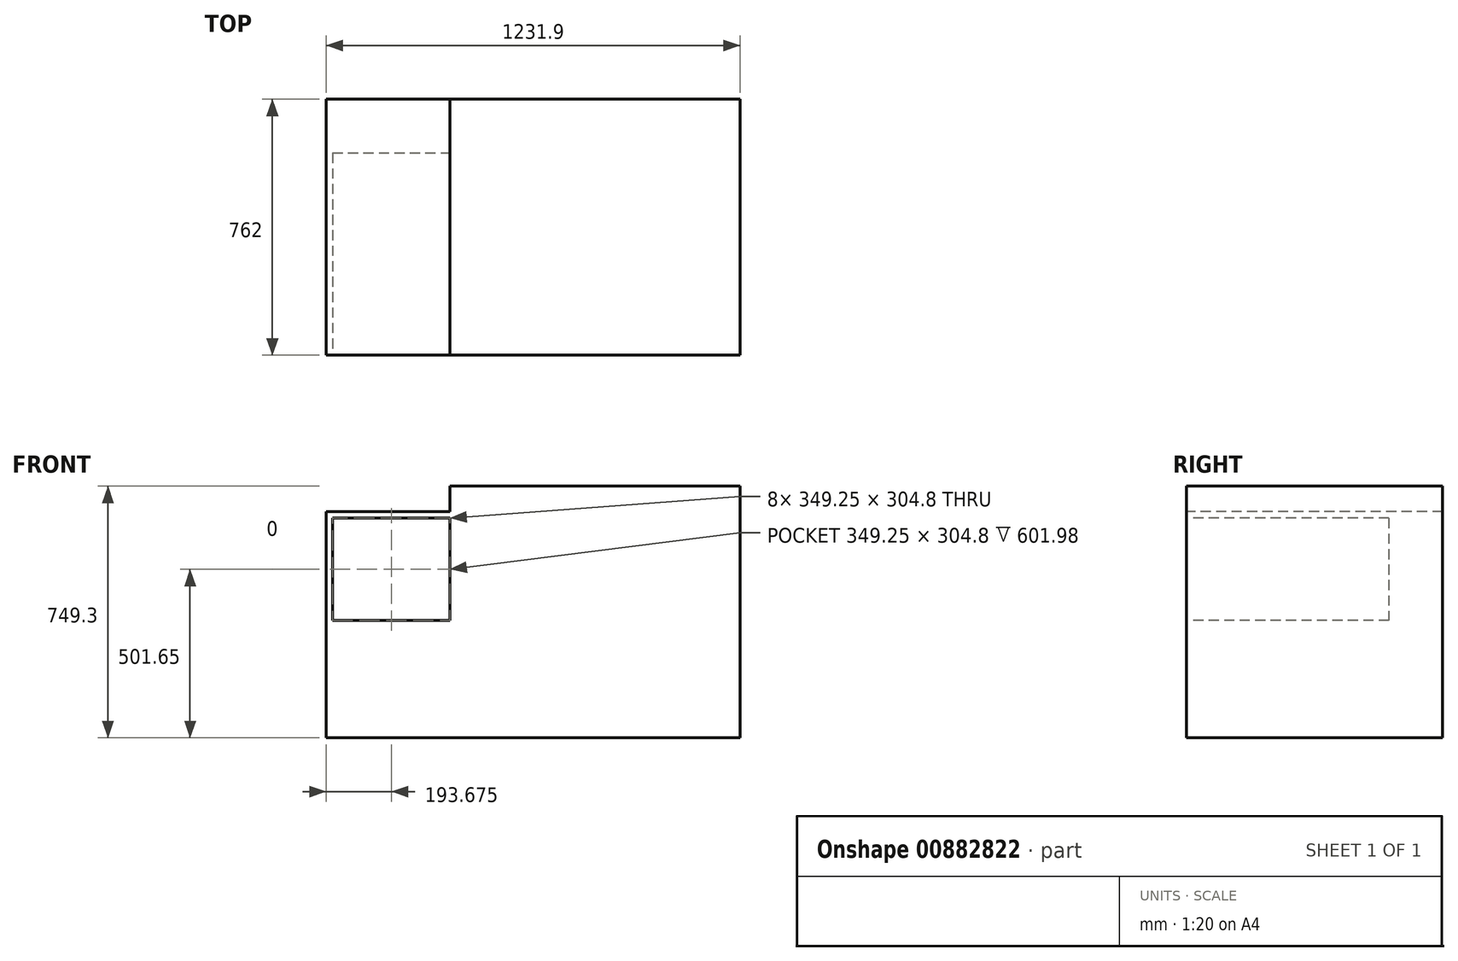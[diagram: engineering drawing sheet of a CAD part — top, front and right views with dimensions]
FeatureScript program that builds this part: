
annotation { "Feature Type Name" : "Feature", "Feature Type Description" : "" }
export const myFeature = defineFeature(function(context is Context, id is Id, definition is map)
    precondition{}
    {
        {
            var Q0;
            Q0=qCreatedBy(makeId("Top.planeOp"),FACE);
            var sketch = newSketch(context, id + "F0", { "sketchPlane" : qUnion([Q0])});
            skLineSegment(sketch, "E0.bottom", {"start": v(615.95, 381) * mm, "end": v(-615.95, 381) * mm});
            skLineSegment(sketch, "E0.top", {"start": v(615.95, -381) * mm, "end": v(-615.95, -381) * mm});
            skLineSegment(sketch, "E0.left", {"start": v(615.95, 381) * mm, "end": v(615.95, -381) * mm});
            skLineSegment(sketch, "E0.right", {"start": v(-615.95, 381) * mm, "end": v(-615.95, -381) * mm});
            skPoint(sketch, "E0.middle", {"position": v(0, 0) * mm});
            skSolve(sketch);
        }
        {
            var Q0;
            Q0=makeQuery(id+"F0.imprint","IMPRINT",FACE,{"disambiguationData":[TD([[makeQuery(id+"F0.imprint","IMPRINT",EDGE,{"derivedFrom":sQuery(id+"F0.wireOp",EDGE,"E0.bottom")}),1.0]])]});
            extrude(context, id + "F1", {"entities" : qUnion([Q0]), "depth" : 749.3 * mm, "offsetDistance" : 25.4 * mm});
        }
        {
            var Q0;
            Q0=makeQuery(id+"F1.opExtrude","CAP_FACE",FACE,{"disambiguationData":[OSD([sQuery(id+"F0.wireOp",EDGE,"E0.bottom"),sQuery(id+"F0.wireOp",EDGE,"E0.top"),sQuery(id+"F0.wireOp",EDGE,"E0.left"),sQuery(id+"F0.wireOp",EDGE,"E0.right")])],"isStart":false});
            var sketch = newSketch(context, id + "F2", { "sketchPlane" : qUnion([Q0])});
            skLineSegment(sketch, "E1.bottom", {"start": v(-615.95, -381) * mm, "end": v(-247.65, -381) * mm});
            skLineSegment(sketch, "E1.top", {"start": v(-615.95, 381) * mm, "end": v(-247.65, 381) * mm});
            skLineSegment(sketch, "E1.left", {"start": v(-615.95, -381) * mm, "end": v(-615.95, 381) * mm});
            skLineSegment(sketch, "E1.right", {"start": v(-247.65, -381) * mm, "end": v(-247.65, 381) * mm});
            skSolve(sketch);
        }
        {
            var Q0;
            Q0=makeQuery(id+"F2.imprint","IMPRINT",FACE,{"disambiguationData":[TD([[makeQuery(id+"F2.imprint","IMPRINT",EDGE,{"derivedFrom":sQuery(id+"F2.wireOp",EDGE,"E1.bottom")}),-1.0]])]});
            extrude(context, id + "F3", {"entities" : qUnion([Q0]), "operationType" : NewBodyOperationType.REMOVE, "oppositeDirection" : true, "depth" : 76.2 * mm, "offsetDistance" : 25.4 * mm});
        }
        {
            var Q0;
            Q0=makeQuery(id+"F1.opExtrude","SWEPT_FACE",FACE,{"disambiguationData":[OSD([sQuery(id+"F0.wireOp",EDGE,"E0.top")])]});
            var sketch = newSketch(context, id + "F4", { "sketchPlane" : qUnion([Q0])});
            skLineSegment(sketch, "E2", {"start": v(596.9, 0) * mm, "end": v(-215.9, 0) * mm});
            skPoint(sketch, "E3.endSnap0", {"position": v(184.15, 749.3) * mm});
            skLineSegment(sketch, "E4.bottom", {"start": v(-215.9, 0) * mm, "end": v(596.9, 0) * mm});
            skLineSegment(sketch, "E4.top", {"start": v(-215.9, 730.25) * mm, "end": v(596.9, 730.25) * mm});
            skLineSegment(sketch, "E4.left", {"start": v(-215.9, 0) * mm, "end": v(-215.9, 730.25) * mm});
            skLineSegment(sketch, "E4.right", {"start": v(596.9, 0) * mm, "end": v(596.9, 730.25) * mm});
            skLineSegment(sketch, "E5.bottom", {"start": v(-615.95, 673.1) * mm, "end": v(-596.9, 673.1) * mm});
            skLineSegment(sketch, "E5.top", {"start": v(-615.95, 654.05) * mm, "end": v(-596.9, 654.05) * mm});
            skLineSegment(sketch, "E5.left", {"start": v(-615.95, 673.1) * mm, "end": v(-615.95, 654.05) * mm});
            skLineSegment(sketch, "E5.right", {"start": v(-596.9, 673.1) * mm, "end": v(-596.9, 654.05) * mm});
            skLineSegment(sketch, "E6.bottom", {"start": v(-596.9, 654.05) * mm, "end": v(-247.65, 654.05) * mm});
            skLineSegment(sketch, "E6.top", {"start": v(-596.9, 349.25) * mm, "end": v(-247.65, 349.25) * mm});
            skLineSegment(sketch, "E6.left", {"start": v(-596.9, 654.05) * mm, "end": v(-596.9, 349.25) * mm});
            skLineSegment(sketch, "E6.right", {"start": v(-215.9, 654.05) * mm, "end": v(-215.9, 349.25) * mm});
            skLineSegment(sketch, "E7.left", {"start": v(-215.9, 654.05) * mm, "end": v(-215.9, 328.72) * mm});
            skLineSegment(sketch, "E7.right", {"start": v(-247.65, 654.05) * mm, "end": v(-247.65, 349.25) * mm});
            skPoint(sketch, "E8.orphan", {"position": v(-247.65, 328.72) * mm});
            skSolve(sketch);
        }
        {
            var Q0;
            Q0=makeQuery(id+"F4.imprint","IMPRINT",FACE,{"disambiguationData":[TD([[makeQuery(id+"F4.imprint","IMPRINT",EDGE,{"derivedFrom":sQuery(id+"F4.wireOp",EDGE,"E4.bottom")}),-1.0]])]});
            var Q1;
            Q1=makeQuery(id+"F4.imprint","IMPRINT",FACE,{"disambiguationData":[TD([[makeQuery(id+"F4.imprint","IMPRINT",EDGE,{"derivedFrom":sQuery(id+"F4.wireOp",EDGE,"E6.bottom")}),-1.0]])]});
            extrude(context, id + "F5", {"entities" : qUnion([Q0, Q1]), "operationType" : NewBodyOperationType.REMOVE, "oppositeDirection" : true, "depth" : 601.98 * mm, "offsetDistance" : 25.4 * mm});
        }
    });
